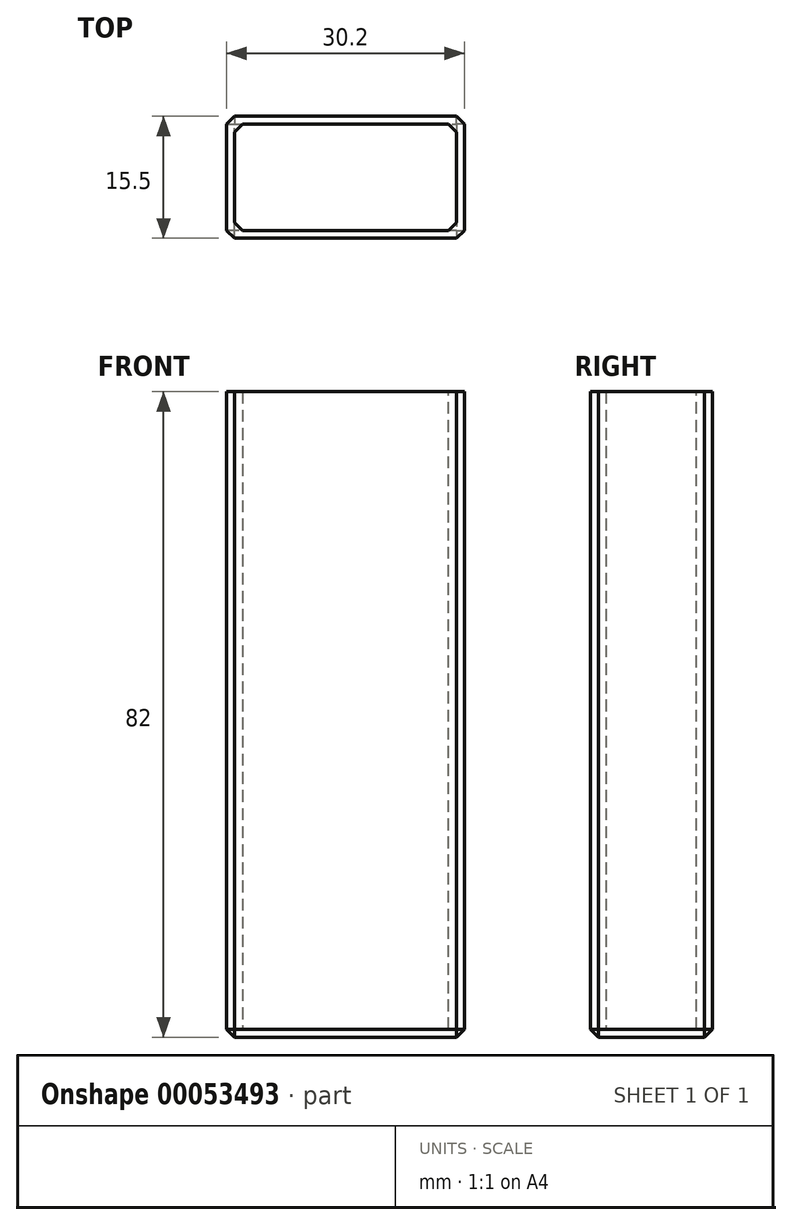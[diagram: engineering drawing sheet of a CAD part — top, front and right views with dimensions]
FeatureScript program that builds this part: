
annotation { "Feature Type Name" : "Feature", "Feature Type Description" : "" }
export const myFeature = defineFeature(function(context is Context, id is Id, definition is map)
    precondition{}
    {
        {
            var Q0;
            Q0=qCreatedBy(makeId("Top.planeOp"),FACE);
            var sketch = newSketch(context, id + "F0", { "sketchPlane" : qUnion([Q0])});
            skLineSegment(sketch, "E0.bottom", {"start": v(-10.5, 0.01) * mm, "end": v(19.7, 0.01) * mm});
            skLineSegment(sketch, "E0.top", {"start": v(-10.5, -15.49) * mm, "end": v(19.7, -15.49) * mm});
            skLineSegment(sketch, "E0.left", {"start": v(-10.5, 0.01) * mm, "end": v(-10.5, -15.49) * mm});
            skLineSegment(sketch, "E0.right", {"start": v(19.7, 0.01) * mm, "end": v(19.7, -15.49) * mm});
            skSolve(sketch);
        }
        {
            var Q0;
            Q0=makeQuery(id+"F0.imprint","IMPRINT",FACE,{"disambiguationData":[TD([[makeQuery(id+"F0.imprint","IMPRINT",EDGE,{"derivedFrom":sQuery(id+"F0.wireOp",EDGE,"E0.bottom")}),-1.0]])]});
            extrude(context, id + "F1", {"entities" : qUnion([Q0]), "depth" : 82 * mm});
        }
        {
            var Q0;
            Q0=makeQuery(id+"F1.opExtrude","CAP_FACE",FACE,{"disambiguationData":[OSD([sQuery(id+"F0.wireOp",EDGE,"E0.bottom"),sQuery(id+"F0.wireOp",EDGE,"E0.top"),sQuery(id+"F0.wireOp",EDGE,"E0.left"),sQuery(id+"F0.wireOp",EDGE,"E0.right")])],"isStart":false});
            shell(context, id + "F2", {"entities" : qUnion([Q0]), "thickness" : 1 * mm});
        }
        {
            var Q0;
            Q0=makeQuery(id+"F1.opExtrude","SWEPT_EDGE",EDGE,{"disambiguationData":[OSD([sQuery(id+"F0.wireOp",EDGE,"E0.bottom"),sQuery(id+"F0.wireOp",EDGE,"E0.right")])]});
            var Q1;
            Q1=makeQuery(id+"F1.opExtrude","SWEPT_EDGE",EDGE,{"disambiguationData":[OSD([sQuery(id+"F0.wireOp",EDGE,"E0.top"),sQuery(id+"F0.wireOp",EDGE,"E0.right")])]});
            var Q2;
            Q2=makeQuery(id+"F1.opExtrude","SWEPT_EDGE",EDGE,{"disambiguationData":[OSD([sQuery(id+"F0.wireOp",EDGE,"E0.bottom"),sQuery(id+"F0.wireOp",EDGE,"E0.left")])]});
            var Q3;
            Q3=makeQuery(id+"F1.opExtrude","SWEPT_EDGE",EDGE,{"disambiguationData":[OSD([sQuery(id+"F0.wireOp",EDGE,"E0.top"),sQuery(id+"F0.wireOp",EDGE,"E0.left")])]});
            var Q4;
            Q4=makeQuery(id+"F1.opExtrude","CAP_EDGE",EDGE,{"disambiguationData":[OSD([sQuery(id+"F0.wireOp",EDGE,"E0.bottom")])],"isStart":true});
            var Q5;
            Q5=makeQuery(id+"F1.opExtrude","CAP_EDGE",EDGE,{"disambiguationData":[OSD([sQuery(id+"F0.wireOp",EDGE,"E0.right")])],"isStart":true});
            var Q6;
            Q6=makeQuery(id+"F1.opExtrude","CAP_EDGE",EDGE,{"disambiguationData":[OSD([sQuery(id+"F0.wireOp",EDGE,"E0.top")])],"isStart":true});
            var Q7;
            Q7=makeQuery(id+"F1.opExtrude","CAP_EDGE",EDGE,{"disambiguationData":[OSD([sQuery(id+"F0.wireOp",EDGE,"E0.left")])],"isStart":true});
            chamfer(context, id + "F3", {"entities" : qUnion([Q0, Q1, Q2, Q3, Q4, Q5, Q6, Q7]), "width" : 1 * mm, "tangentPropagation" : true});
        }
        {
            var Q0;
            Q0=makeQuery(id+"F2.opShell","OFFSET_EDGE",EDGE,{"disambiguationData":[OSD([sQuery(id+"F0.wireOp",EDGE,"E0.bottom"),sQuery(id+"F0.wireOp",EDGE,"E0.left")])]});
            var Q1;
            Q1=makeQuery(id+"F2.opShell","OFFSET_EDGE",EDGE,{"disambiguationData":[OSD([sQuery(id+"F0.wireOp",EDGE,"E0.bottom"),sQuery(id+"F0.wireOp",EDGE,"E0.right")])]});
            var Q2;
            Q2=makeQuery(id+"F2.opShell","OFFSET_EDGE",EDGE,{"disambiguationData":[OSD([sQuery(id+"F0.wireOp",EDGE,"E0.top"),sQuery(id+"F0.wireOp",EDGE,"E0.right")])]});
            var Q3;
            Q3=makeQuery(id+"F2.opShell","OFFSET_EDGE",EDGE,{"disambiguationData":[OSD([sQuery(id+"F0.wireOp",EDGE,"E0.top"),sQuery(id+"F0.wireOp",EDGE,"E0.left")])]});
            chamfer(context, id + "F4", {"entities" : qUnion([Q0, Q1, Q2, Q3]), "width" : 1 * mm, "tangentPropagation" : true});
        }
    });
